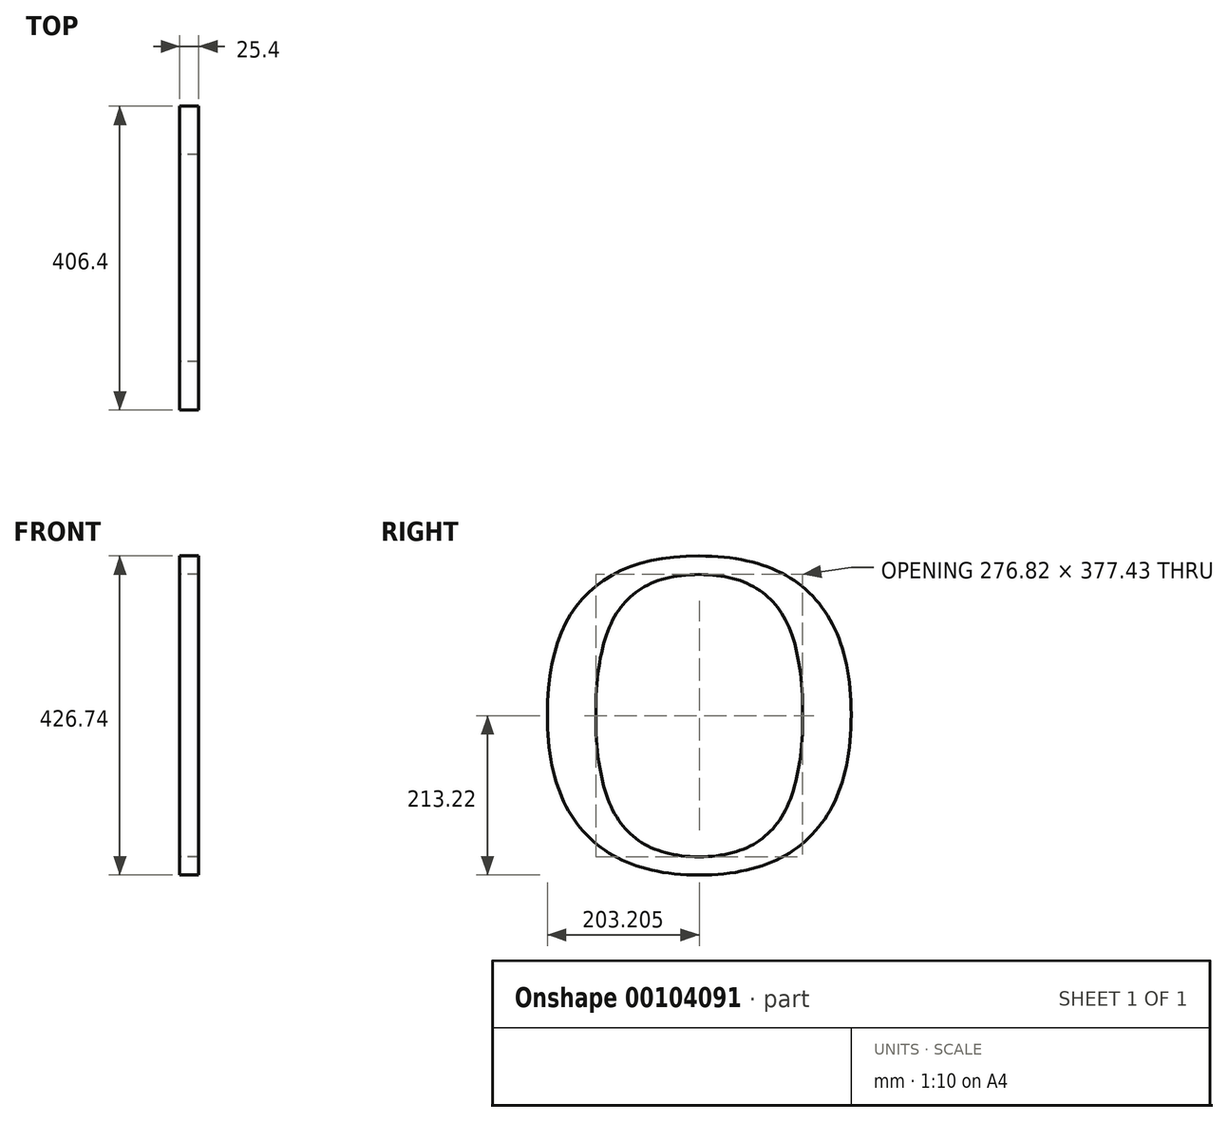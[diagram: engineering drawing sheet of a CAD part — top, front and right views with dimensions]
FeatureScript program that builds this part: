
annotation { "Feature Type Name" : "Feature", "Feature Type Description" : "" }
export const myFeature = defineFeature(function(context is Context, id is Id, definition is map)
    precondition{}
    {
        {
            var Q0;
            Q0=qCreatedBy(makeId("Right.planeOp"),FACE);
            var sketch = newSketch(context, id + "F0", { "sketchPlane" : qUnion([Q0])});
            skText(sketch, "E0", { "text": "O", "fontName": "Tinos-Regular.ttf"});
            const initialGuessF0  = {"E0": [-0.4325, 0, 1, 0, 0.4572]};
            skSetInitialGuess(sketch, initialGuessF0);
            skSolve(sketch);
        }
        {
            var Q0;
            Q0 = qSketchRegion(id + "F0", true);
            extrude(context, id + "F1", {"entities" : qUnion([Q0]), "depth" : 25.4 * mm});
        }
    });
